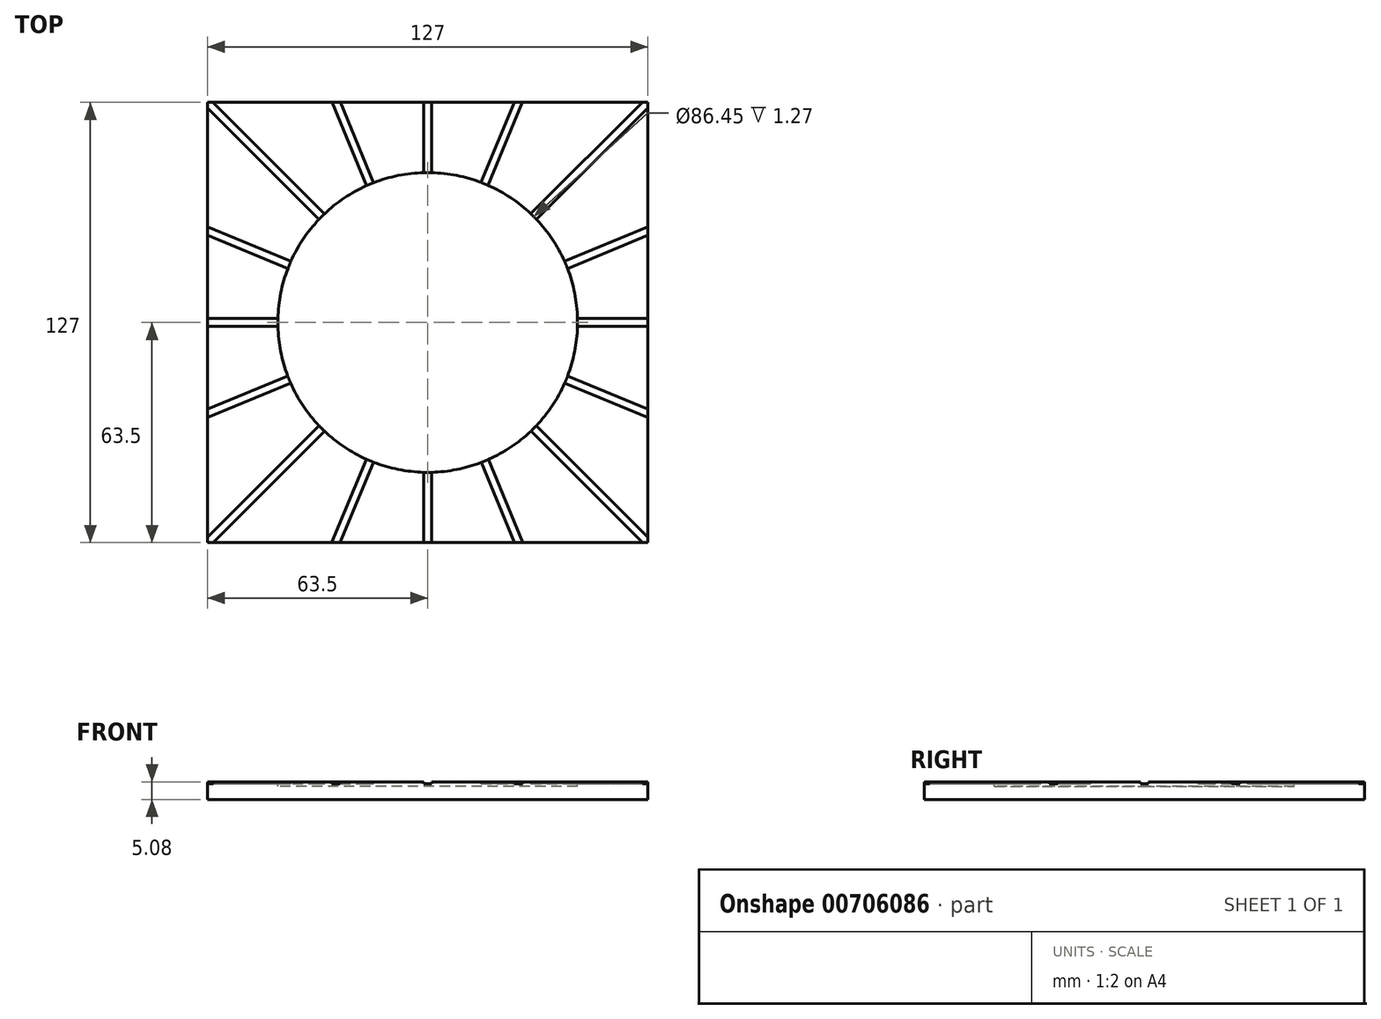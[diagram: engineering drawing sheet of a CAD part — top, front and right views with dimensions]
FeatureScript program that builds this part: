
annotation { "Feature Type Name" : "Feature", "Feature Type Description" : "" }
export const myFeature = defineFeature(function(context is Context, id is Id, definition is map)
    precondition{}
    {
        {
            var Q0;
            Q0=qCreatedBy(makeId("Top.planeOp"),FACE);
            var sketch = newSketch(context, id + "F0", { "sketchPlane" : qUnion([Q0])});
            skLineSegment(sketch, "E0.bottom", {"start": v(63.5, -63.5) * mm, "end": v(-63.5, -63.5) * mm});
            skLineSegment(sketch, "E0.top", {"start": v(63.5, 63.5) * mm, "end": v(-63.5, 63.5) * mm});
            skLineSegment(sketch, "E0.left", {"start": v(63.5, -63.5) * mm, "end": v(63.5, 63.5) * mm});
            skLineSegment(sketch, "E0.right", {"start": v(-63.5, -63.5) * mm, "end": v(-63.5, 63.5) * mm});
            skPoint(sketch, "E0.middle", {"position": v(0, 0) * mm});
            skSolve(sketch);
        }
        {
            var Q0;
            Q0=qSketchRegion(id+"F0",true);
            extrude(context, id + "F1", {"entities" : qUnion([Q0]), "depth" : 5.08 * mm, "offsetDistance" : 25.4 * mm});
        }
        {
            var Q0;
            Q0=makeQuery(id+"F1.opExtrude","CAP_FACE",FACE,{"disambiguationData":[OSD([sQuery(id+"F0.wireOp",EDGE,"E0.bottom"),sQuery(id+"F0.wireOp",EDGE,"E0.top"),sQuery(id+"F0.wireOp",EDGE,"E0.left"),sQuery(id+"F0.wireOp",EDGE,"E0.right")])],"isStart":false});
            var sketch = newSketch(context, id + "F2", { "sketchPlane" : qUnion([Q0])});
            skLineSegment(sketch, "E1.right", {"start": v(90.22, -1.12) * mm, "end": v(90.22, 1.12) * mm});
            skPoint(sketch, "E1.middle", {"position": v(0, 0) * mm});
            skLineSegment(sketch, "E2.bottom", {"start": v(-1.1, -90.22) * mm, "end": v(1.1, -90.22) * mm});
            skLineSegment(sketch, "E2.top", {"start": v(-1.1, 90.22) * mm, "end": v(1.1, 90.22) * mm});
            skLineSegment(sketch, "E3", {"start": v(1.1, 90.22) * mm, "end": v(1.1, 38.17) * mm});
            skLineSegment(sketch, "E4", {"start": v(1.1, 38.17) * mm, "end": v(-1.1, 38.17) * mm});
            skLineSegment(sketch, "E5", {"start": v(-1.1, 38.17) * mm, "end": v(-1.1, 90.22) * mm});
            skLineSegment(sketch, "E6", {"start": v(90.22, -1.12) * mm, "end": v(38.17, -1.12) * mm});
            skLineSegment(sketch, "E7", {"start": v(38.17, -1.12) * mm, "end": v(38.14, 1.12) * mm});
            skLineSegment(sketch, "E8", {"start": v(38.14, 1.12) * mm, "end": v(90.22, 1.12) * mm});
            skLineSegment(sketch, "E9", {"start": v(1.1, -90.22) * mm, "end": v(1.1, -38.17) * mm});
            skLineSegment(sketch, "E10", {"start": v(1.1, -38.17) * mm, "end": v(-1.1, -38.17) * mm});
            skLineSegment(sketch, "E11", {"start": v(-1.1, -38.17) * mm, "end": v(-1.1, -90.22) * mm});
            skLineSegment(sketch, "E12", {"start": v(-90.22, 1.12) * mm, "end": v(-90.22, -1.12) * mm});
            skLineSegment(sketch, "E13", {"start": v(-90.22, -1.12) * mm, "end": v(-38.17, -1.12) * mm});
            skLineSegment(sketch, "E14", {"start": v(-38.17, -1.12) * mm, "end": v(-38.17, 1.12) * mm});
            skLineSegment(sketch, "E15", {"start": v(-38.17, 1.12) * mm, "end": v(-90.22, 1.12) * mm});
            skLineSegment(sketch, "E16.right", {"start": v(64.57, 63) * mm, "end": v(63, 64.58) * mm});
            skPoint(sketch, "E16.middle", {"position": v(-0.01, 0) * mm});
            skLineSegment(sketch, "E17.bottom", {"start": v(63, -64.57) * mm, "end": v(64.56, -63.02) * mm});
            skLineSegment(sketch, "E17.top", {"start": v(-64.58, 63.01) * mm, "end": v(-63.03, 64.56) * mm});
            skLineSegment(sketch, "E18", {"start": v(-63.03, 64.56) * mm, "end": v(-26.22, 27.76) * mm});
            skLineSegment(sketch, "E19", {"start": v(-26.22, 27.76) * mm, "end": v(-27.78, 26.2) * mm});
            skLineSegment(sketch, "E20", {"start": v(-27.78, 26.2) * mm, "end": v(-64.58, 63.01) * mm});
            skLineSegment(sketch, "E21", {"start": v(64.57, 63) * mm, "end": v(27.77, 26.2) * mm});
            skLineSegment(sketch, "E22", {"start": v(27.77, 26.2) * mm, "end": v(26.16, 27.75) * mm});
            skLineSegment(sketch, "E23", {"start": v(26.16, 27.75) * mm, "end": v(63, 64.58) * mm});
            skLineSegment(sketch, "E24", {"start": v(64.56, -63.02) * mm, "end": v(27.76, -26.22) * mm});
            skLineSegment(sketch, "E25", {"start": v(27.76, -26.22) * mm, "end": v(26.2, -27.77) * mm});
            skLineSegment(sketch, "E26", {"start": v(26.2, -27.77) * mm, "end": v(63, -64.57) * mm});
            skLineSegment(sketch, "E27", {"start": v(-64.6, -63) * mm, "end": v(-63.01, -64.59) * mm});
            skLineSegment(sketch, "E28", {"start": v(-63.01, -64.59) * mm, "end": v(-26.2, -27.79) * mm});
            skLineSegment(sketch, "E29", {"start": v(-26.2, -27.79) * mm, "end": v(-27.8, -26.2) * mm});
            skLineSegment(sketch, "E30", {"start": v(-27.8, -26.2) * mm, "end": v(-64.6, -63) * mm});
            skLineSegment(sketch, "E31.right", {"start": v(83.7, 33.54) * mm, "end": v(82.84, 35.61) * mm});
            skPoint(sketch, "E31.middle", {"position": v(-0.08, 0.05) * mm});
            skLineSegment(sketch, "E32.bottom", {"start": v(33.43, -83.72) * mm, "end": v(35.46, -82.88) * mm});
            skLineSegment(sketch, "E32.top", {"start": v(-35.62, 82.98) * mm, "end": v(-33.59, 83.82) * mm});
            skLineSegment(sketch, "E33", {"start": v(-33.59, 83.82) * mm, "end": v(-13.67, 35.74) * mm});
            skLineSegment(sketch, "E34", {"start": v(-13.67, 35.74) * mm, "end": v(-15.7, 34.9) * mm});
            skLineSegment(sketch, "E35", {"start": v(-15.7, 34.9) * mm, "end": v(-35.62, 82.98) * mm});
            skLineSegment(sketch, "E36", {"start": v(83.7, 33.54) * mm, "end": v(35.61, 13.62) * mm});
            skLineSegment(sketch, "E37", {"start": v(35.61, 13.62) * mm, "end": v(34.73, 15.68) * mm});
            skLineSegment(sketch, "E38", {"start": v(34.73, 15.68) * mm, "end": v(82.84, 35.61) * mm});
            skLineSegment(sketch, "E39", {"start": v(35.46, -82.88) * mm, "end": v(15.54, -34.8) * mm});
            skLineSegment(sketch, "E40", {"start": v(15.54, -34.8) * mm, "end": v(13.51, -35.63) * mm});
            skLineSegment(sketch, "E41", {"start": v(13.51, -35.63) * mm, "end": v(33.43, -83.72) * mm});
            skLineSegment(sketch, "E42", {"start": v(-83.86, -33.44) * mm, "end": v(-83, -35.5) * mm});
            skLineSegment(sketch, "E43", {"start": v(-83, -35.5) * mm, "end": v(-34.91, -15.59) * mm});
            skLineSegment(sketch, "E44", {"start": v(-34.91, -15.59) * mm, "end": v(-35.77, -13.52) * mm});
            skLineSegment(sketch, "E45", {"start": v(-35.77, -13.52) * mm, "end": v(-83.86, -33.44) * mm});
            skLineSegment(sketch, "E46.right", {"start": v(82.82, -35.45) * mm, "end": v(83.67, -33.38) * mm});
            skPoint(sketch, "E46.middle", {"position": v(-0.1, 0.1) * mm});
            skLineSegment(sketch, "E47.bottom", {"start": v(-35.64, -82.82) * mm, "end": v(-33.61, -83.66) * mm});
            skLineSegment(sketch, "E47.top", {"start": v(33.4, 83.88) * mm, "end": v(35.43, 83.04) * mm});
            skLineSegment(sketch, "E48", {"start": v(35.43, 83.04) * mm, "end": v(15.52, 34.95) * mm});
            skLineSegment(sketch, "E49", {"start": v(15.52, 34.95) * mm, "end": v(13.49, 35.8) * mm});
            skLineSegment(sketch, "E50", {"start": v(13.49, 35.8) * mm, "end": v(33.4, 83.88) * mm});
            skLineSegment(sketch, "E51", {"start": v(82.82, -35.45) * mm, "end": v(34.73, -15.53) * mm});
            skLineSegment(sketch, "E52", {"start": v(34.73, -15.53) * mm, "end": v(35.56, -13.45) * mm});
            skLineSegment(sketch, "E53", {"start": v(35.56, -13.45) * mm, "end": v(83.67, -33.38) * mm});
            skLineSegment(sketch, "E54", {"start": v(-33.61, -83.66) * mm, "end": v(-13.7, -35.58) * mm});
            skLineSegment(sketch, "E55", {"start": v(-13.7, -35.58) * mm, "end": v(-15.72, -34.74) * mm});
            skLineSegment(sketch, "E56", {"start": v(-15.72, -34.74) * mm, "end": v(-35.64, -82.82) * mm});
            skLineSegment(sketch, "E57", {"start": v(-83.02, 35.67) * mm, "end": v(-83.88, 33.6) * mm});
            skLineSegment(sketch, "E58", {"start": v(-83.88, 33.6) * mm, "end": v(-35.8, 13.68) * mm});
            skLineSegment(sketch, "E59", {"start": v(-35.8, 13.68) * mm, "end": v(-34.94, 15.75) * mm});
            skLineSegment(sketch, "E60", {"start": v(-34.94, 15.75) * mm, "end": v(-83.02, 35.67) * mm});
            skSolve(sketch);
        }
        {
            var Q0;
            Q0=qSketchRegion(id+"F2",true);
            extrude(context, id + "F3", {"entities" : qUnion([Q0]), "operationType" : NewBodyOperationType.REMOVE, "oppositeDirection" : true, "depth" : 0.5 * mm, "offsetDistance" : 25.4 * mm});
        }
        {
            var Q0;
            Q0=makeQuery(id+"F1.opExtrude","CAP_FACE",FACE,{"disambiguationData":[OSD([sQuery(id+"F0.wireOp",EDGE,"E0.bottom"),sQuery(id+"F0.wireOp",EDGE,"E0.top"),sQuery(id+"F0.wireOp",EDGE,"E0.left"),sQuery(id+"F0.wireOp",EDGE,"E0.right")])],"isStart":false});
            var sketch = newSketch(context, id + "F4", { "sketchPlane" : qUnion([Q0])});
            skCircle(sketch, "E61", {"center": v(0, 0) * mm, "radius": 43.23 * mm});
            skSolve(sketch);
        }
        {
            var Q0;
            Q0 = qSketchRegion(id + "F4", true);
            extrude(context, id + "F5", {"entities" : qUnion([Q0]), "operationType" : NewBodyOperationType.REMOVE, "oppositeDirection" : true, "depth" : 1.27 * mm, "offsetDistance" : 25.4 * mm});
        }
    });
